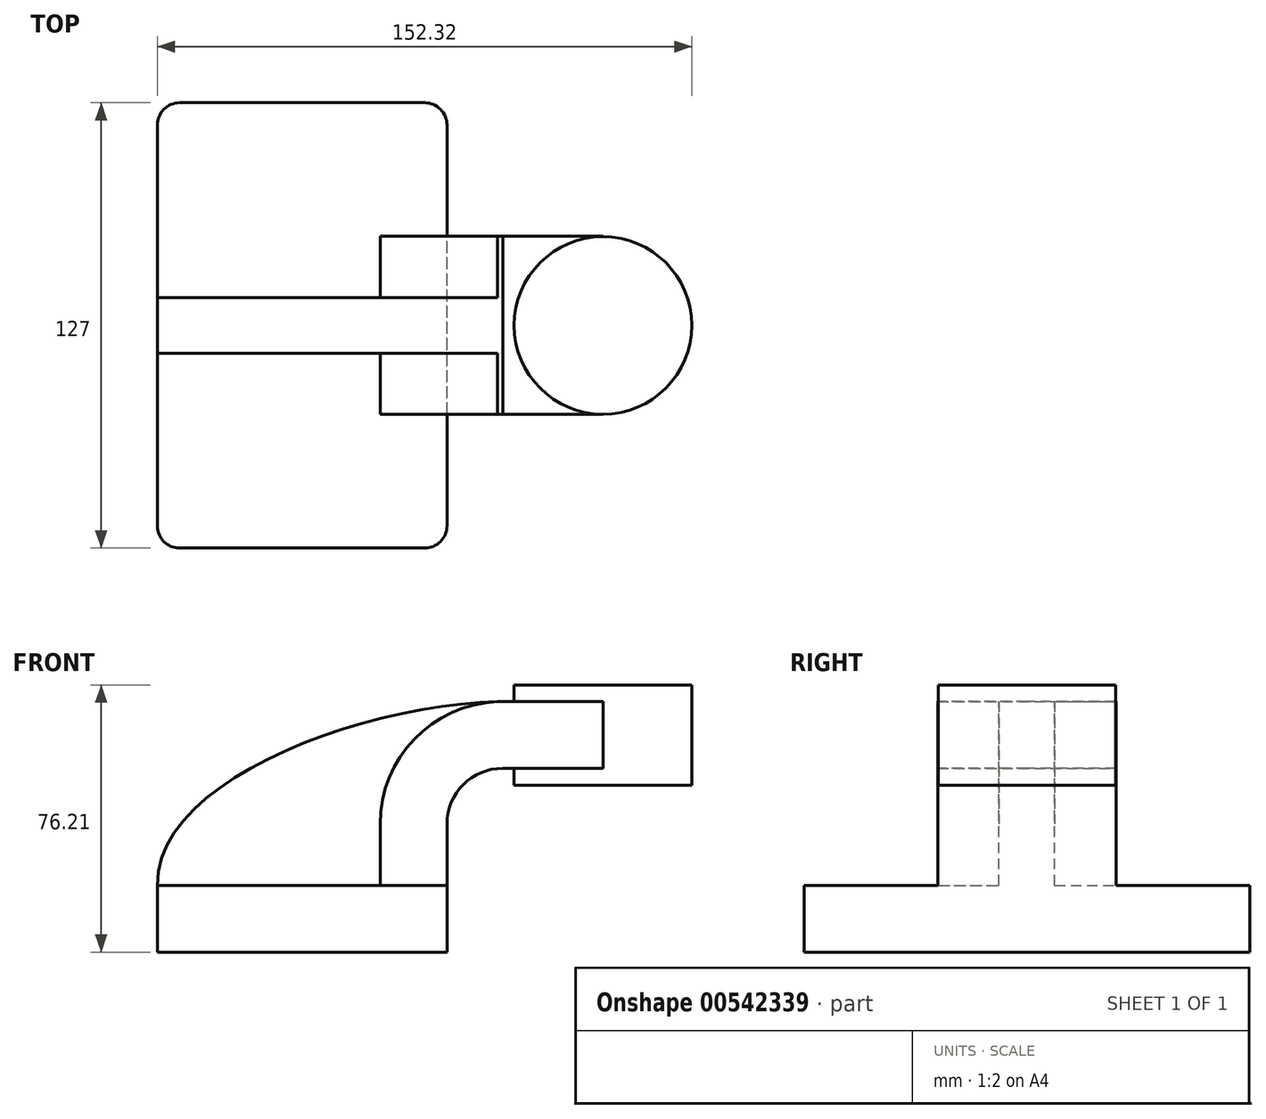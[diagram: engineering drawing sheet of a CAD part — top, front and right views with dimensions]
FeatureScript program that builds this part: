
annotation { "Feature Type Name" : "Feature", "Feature Type Description" : "" }
export const myFeature = defineFeature(function(context is Context, id is Id, definition is map)
    precondition{}
    {
        {
            var Q0;
            Q0=qCreatedBy(makeId("Front.planeOp"),FACE);
            var sketch = newSketch(context, id + "F0", { "sketchPlane" : qUnion([Q0])});
            skLineSegment(sketch, "E0.bottom", {"start": v(-41.28, 9.52) * mm, "end": v(41.27, 9.53) * mm});
            skLineSegment(sketch, "E0.top", {"start": v(-41.28, -9.53) * mm, "end": v(41.28, -9.53) * mm});
            skLineSegment(sketch, "E0.left", {"start": v(-41.28, 9.52) * mm, "end": v(-41.28, -9.53) * mm});
            skLineSegment(sketch, "E0.right", {"start": v(41.27, 9.53) * mm, "end": v(41.28, -9.52) * mm});
            skPoint(sketch, "E0.middle", {"position": v(0, 0) * mm});
            skLineSegment(sketch, "E1", {"start": v(41.27, 9.53) * mm, "end": v(41.27, 27) * mm});
            skArc(sketch, "E2", {"start": v(41.27, 27) * mm, "mid": v(45.92, 38.23) * mm, "end": v(57.15, 42.88) * mm});
            skLineSegment(sketch, "E3", {"start": v(57.15, 42.88) * mm, "end": v(85.73, 42.88) * mm});
            skLineSegment(sketch, "E4.bottom", {"start": v(60.24, 66.67) * mm, "end": v(111.04, 66.67) * mm});
            skLineSegment(sketch, "E4.top", {"start": v(60.24, 38.1) * mm, "end": v(111.04, 38.1) * mm});
            skLineSegment(sketch, "E4.left", {"start": v(60.24, 66.67) * mm, "end": v(60.24, 38.1) * mm});
            skLineSegment(sketch, "E4.right", {"start": v(111.04, 66.67) * mm, "end": v(111.04, 38.1) * mm});
            skPoint(sketch, "E4.middle", {"position": v(85.64, 52.39) * mm});
            skLineSegment(sketch, "E5.0", {"start": v(57.15, 61.93) * mm, "end": v(85.73, 61.93) * mm});
            skArc(sketch, "E5.1", {"start": v(22.22, 27) * mm, "mid": v(32.45, 51.7) * mm, "end": v(57.15, 61.93) * mm});
            skLineSegment(sketch, "E5.2", {"start": v(22.22, 9.53) * mm, "end": v(22.22, 27) * mm});
            skLineSegment(sketch, "E6", {"start": v(85.73, 38.1) * mm, "end": v(85.73, 66.67) * mm});
            skFitSpline(sketch, "E7", {"points": [v(-41.28, 9.52) * mm, v(57.15, 61.93) * mm], "startDerivative": vector(-0.68, 92.05) * mm, "endDerivative": vector(115.68, 1.65) * mm});
            skSolve(sketch);
        }
        {
            var Q0;
            Q0=makeQuery(id+"F0.imprint","IMPRINT",FACE,{"disambiguationData":[TD([[makeQuery(id+"F0.imprint","IMPRINT",EDGE,{"derivedFrom":sQuery(id+"F0.wireOp",EDGE,"E0.top")}),1.0]])]});
            extrude(context, id + "F1", {"entities" : qUnion([Q0]), "endBound" : BoundingType.SYMMETRIC, "depth" : 127 * mm, "offsetDistance" : 25.4 * mm});
        }
        {
            var Q0;
            {var subQ4=sQuery(id+"F0.wireOp",EDGE,"E1");Q0=makeQuery(id+"F0.imprint","IMPRINT",FACE,{"disambiguationData":[TD([[makeQuery(id+"F0.imprint","IMPRINT",EDGE,{"derivedFrom":subQ4}),1.0]])]});}
            var Q1;
            {var subQ0=sQuery(id+"F0.wireOp",EDGE,"E6");var subQ1=sQuery(id+"F0.wireOp",EDGE,"E3");var subQ2=makeQuery(id+"F0.imprint","INTERSECT",VERTEX,{"derivedFrom":[subQ1,subQ0]});Q1=makeQuery(id+"F0.imprint","IMPRINT",FACE,{"disambiguationData":[TD([[makeQuery(id+"F0.imprint","IMPRINT",EDGE,{"disambiguationData":[TD([[subQ2,1.0]])],"derivedFrom":subQ1}),1.0]])]});}
            extrude(context, id + "F2", {"entities" : qUnion([Q0, Q1]), "operationType" : NewBodyOperationType.ADD, "endBound" : BoundingType.SYMMETRIC, "depth" : 50.8 * mm, "offsetDistance" : 25.4 * mm});
        }
        {
            var Q0;
            {var subQ3=sQuery(id+"F0.wireOp",EDGE,"E5.2");Q0=makeQuery(id+"F0.imprint","IMPRINT",FACE,{"disambiguationData":[TD([[makeQuery(id+"F0.imprint","IMPRINT",EDGE,{"derivedFrom":subQ3}),1.0]])]});}
            extrude(context, id + "F3", {"entities" : qUnion([Q0]), "operationType" : NewBodyOperationType.ADD, "endBound" : BoundingType.SYMMETRIC, "depth" : 15.88 * mm, "offsetDistance" : 25.4 * mm});
        }
        {
            var Q0;
            {var subQ0=sQuery(id+"F0.wireOp",EDGE,"E4.right");Q0=makeQuery(id+"F0.imprint","IMPRINT",FACE,{"disambiguationData":[TD([[makeQuery(id+"F0.imprint","IMPRINT",EDGE,{"derivedFrom":subQ0}),-1.0]])]});}
            var Q1;
            Q1=sQuery(id+"F0.wireOp",EDGE,"E6");
            revolve(context, id + "F4", {"operationType" : NewBodyOperationType.ADD, "entities" : qUnion([Q0]), "axis" : qUnion([Q1]), "revolveType" : RevolveType.FULL});
        }
        {
            var Q0;
            Q0=makeQuery(id+"F1.opExtrude","CAP_EDGE",EDGE,{"disambiguationData":[OSD([sQuery(id+"F0.wireOp",EDGE,"E0.right")])],"isStart":true});
            var Q1;
            Q1=makeQuery(id+"F1.opExtrude","CAP_EDGE",EDGE,{"disambiguationData":[OSD([sQuery(id+"F0.wireOp",EDGE,"E0.left")])],"isStart":true});
            var Q2;
            Q2=makeQuery(id+"F1.opExtrude","CAP_EDGE",EDGE,{"disambiguationData":[OSD([sQuery(id+"F0.wireOp",EDGE,"E0.left")])],"isStart":false});
            var Q3;
            Q3=makeQuery(id+"F1.opExtrude","CAP_EDGE",EDGE,{"disambiguationData":[OSD([sQuery(id+"F0.wireOp",EDGE,"E0.right")])],"isStart":false});
            fillet(context, id + "F5", {"entities" : qUnion([Q0, Q1, Q2, Q3]), "radius" : 6.35 * mm, "tangentPropagation" : true, "allowEdgeOverflow" : false});
        }
    });
